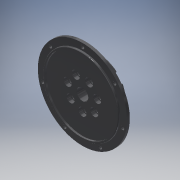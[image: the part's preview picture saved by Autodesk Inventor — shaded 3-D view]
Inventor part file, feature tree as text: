
AUTODESK INVENTOR PART (.ipt)
format: ipt  version: 2018 (Build 220112000, 112)  size: 845,312 bytes
history: native  units: mm
features: sketch x10, extrude x7, thread x7, fillet x2, plane x2, revolve x1, sweep x1, other x1, pattern_circular x1, chamfer x1
ambient origin geometry x8: Origin, YZ Plane, XZ Plane, XY Plane, X Axis, Y Axis, Z Axis, Center Point
bodies: Solid1 (feature_tree)
feature tree (33):
  revolve  "Revolution1"  [1 undecoded]
  extrude  "Extrusion1"  Depth=40.25mm
  fillet  "Fillet1"  Radius=50.0mm
  extrude  "Extrusion2"  Depth=5.2mm
  plane  "Work Plane1"
  extrude  "Extrusion3"  Depth=0.75mm
  extrude  "Extrusion4"  TaperAngle=90.0deg  [1 undecoded]
  sweep  "Sweep1"
  fillet  "Fillet2"  Radius=10.0mm
  plane  "Work Plane2"
  extrude  "Extrusion5"  Depth=2.5mm
  extrude  "Extrusion6"  Depth=7.915mm
  other  "Work Axis1"
  pattern_circular  "Circular Pattern1"  [2 undecoded]
  extrude  "Extrusion7"  Depth=10.0mm TaperAngle=0.0deg
  thread  "Thread1"  [1 undecoded]
  thread  "Thread2"  [1 undecoded]
  thread  "Thread3"  [1 undecoded]
  thread  "Thread4"  [1 undecoded]
  thread  "Thread5"  [1 undecoded]
  thread  "Thread6"  [1 undecoded]
  thread  "Thread7"  [1 undecoded]
  chamfer  "Chamfer1"  Distance=3.0mm
  sketch  "Sketch1"  dims[d0=6.5mm d1=19.0mm]
  sketch  "Sketch2"  dims[d2=40.25mm d3=42.375mm d4=50.0mm]
  sketch  "Sketch3"  dims[d5=3.17mm d6=5.2mm]
  sketch  "Sketch4"  dims[d8=30.0mm d11=0.75mm]
  sketch  "Sketch5"  dims[d12=1.4mm d13=90.0deg]
  sketch  "Sketch6"  dims[d14=10.0mm d15=70.0mm d17=360.0deg d19=10.0mm d20=0.0mm]
  sketch  "Sketch7"  dims[d21=1.0mm d22=2.5mm]
  sketch  "Sketch8"  dims[d23=7.915mm d24=7.915mm]
  sketch  "Sketch9"  dims[d25=50.5mm d26=0.0mm]
  sketch  "Sketch10"  dims[d27=25.0mm d28=5.0mm d29=2.8mm d30=1.4mm d31=0.0mm d32=0.0mm d33=9.0mm d34=17.0mm d35=7.0mm d36=4.2mm d37=0.0mm d38=1.7mm d39=3.5mm d40=3.5mm d41=3.0mm d42=0.0mm d43=0.0mm d44=2.0mm d45=-30.0mm d46=12.15mm d47=2.0mm d48=0.0mm d49=10.42mm d50=5.0mm d51=0.0mm d52=70.0mm d53=360.0deg d55=4.0mm d56=46.0mm d57=70.0mm d59=360.0deg d61=5.0mm d62=0.0mm d63=10.0mm d64=0.0mm d65=10.0mm d66=0.0mm d67=10.0mm d68=0.0mm d69=10.0mm d70=0.0mm d71=10.0mm d72=0.0mm d73=10.0mm d74=0.0mm d75=10.0mm d76=0.0mm d77=0.5mm d78=2.0mm d79=45.0deg]
note: 11 required parameter values undecoded (feature->parameter linkage not recoverable at this tier; creation-order binding heuristic only, values carry confidence <= 0.55)